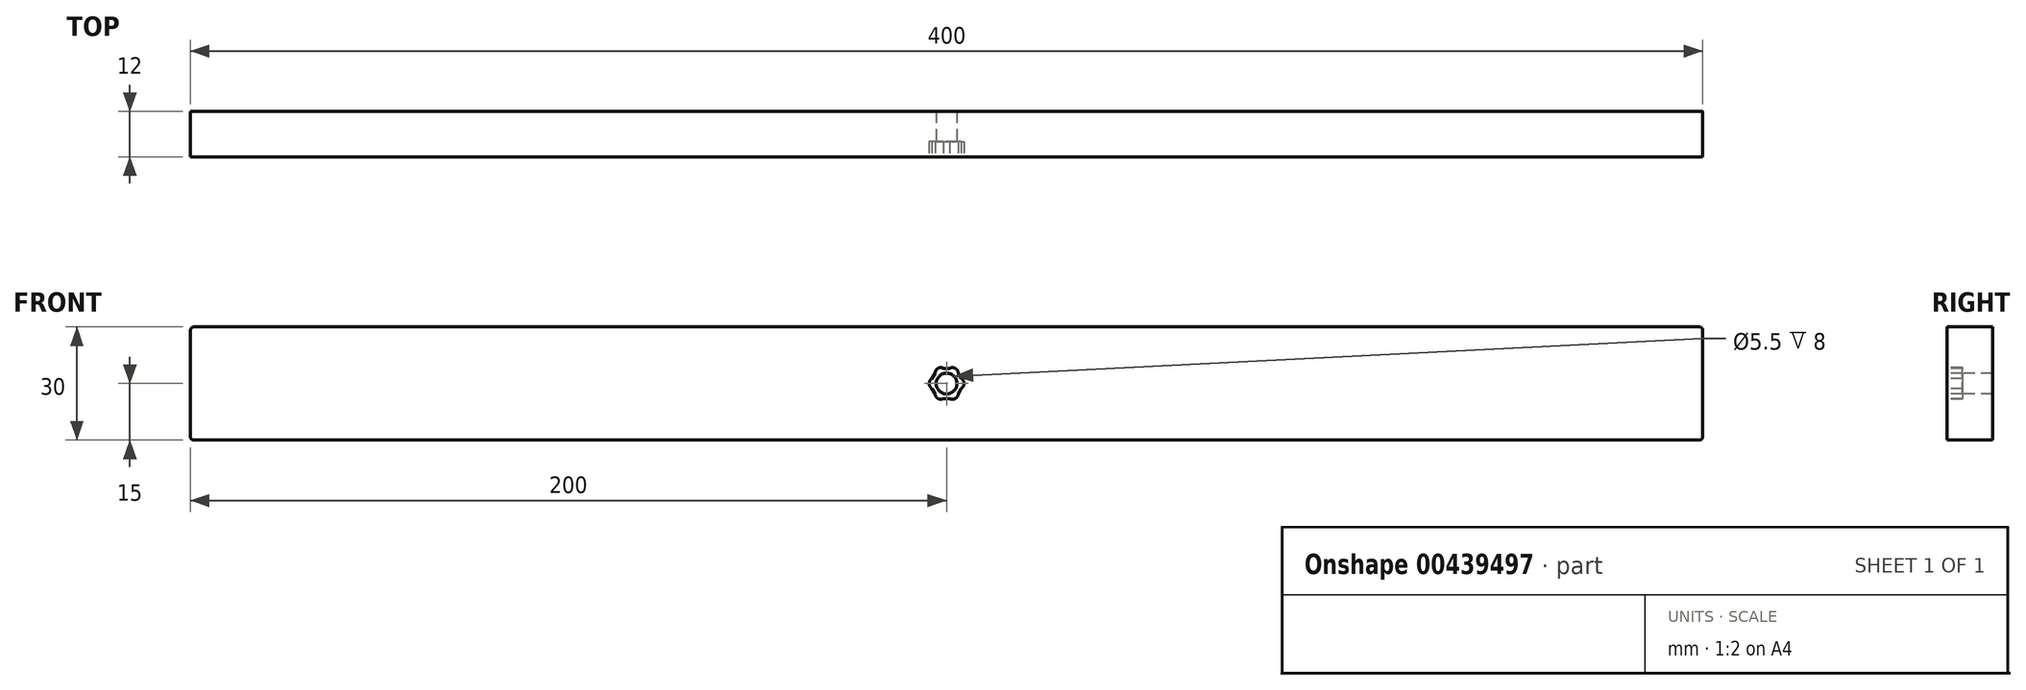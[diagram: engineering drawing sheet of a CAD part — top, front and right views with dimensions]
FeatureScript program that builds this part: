
annotation { "Feature Type Name" : "Feature", "Feature Type Description" : "" }
export const myFeature = defineFeature(function(context is Context, id is Id, definition is map)
    precondition{}
    {
        {
            var Q0;
            Q0=qCreatedBy(makeId("Right.planeOp"),FACE);
            var sketch = newSketch(context, id + "F0", { "sketchPlane" : qUnion([Q0])});
            skLineSegment(sketch, "E0.bottom", {"start": v(0, 0) * mm, "end": v(12, 0) * mm});
            skLineSegment(sketch, "E0.top", {"start": v(0, 30) * mm, "end": v(12, 30) * mm});
            skLineSegment(sketch, "E0.left", {"start": v(0, 0) * mm, "end": v(0, 30) * mm});
            skLineSegment(sketch, "E0.right", {"start": v(12, 0) * mm, "end": v(12, 30) * mm});
            skSolve(sketch);
        }
        {
            var Q0;
            Q0=makeQuery(id+"F0.imprint","IMPRINT",FACE,{"disambiguationData":[TD([[makeQuery(id+"F0.imprint","IMPRINT",EDGE,{"derivedFrom":sQuery(id+"F0.wireOp",EDGE,"E0.bottom")}),1.0]])]});
            extrude(context, id + "F1", {"entities" : qUnion([Q0]), "depth" : 400 * mm, "offsetDistance" : 25 * mm, "symmetric" : true});
        }
        {
            var Q0;
            Q0=makeQuery(id+"F1.opExtrude","CAP_EDGE",EDGE,{"disambiguationData":[OSD([sQuery(id+"F0.wireOp",EDGE,"E0.top")])],"isStart":true});
            var Q1;
            Q1=makeQuery(id+"F1.opExtrude","CAP_EDGE",EDGE,{"disambiguationData":[OSD([sQuery(id+"F0.wireOp",EDGE,"E0.top")])],"isStart":false});
            var Q2;
            Q2=makeQuery(id+"F1.opExtrude","CAP_EDGE",EDGE,{"disambiguationData":[OSD([sQuery(id+"F0.wireOp",EDGE,"E0.bottom")])],"isStart":false});
            var Q3;
            Q3=makeQuery(id+"F1.opExtrude","CAP_EDGE",EDGE,{"disambiguationData":[OSD([sQuery(id+"F0.wireOp",EDGE,"E0.bottom")])],"isStart":true});
            fillet(context, id + "F2", {"entities" : qUnion([Q0, Q1, Q2, Q3]), "tangentPropagation" : true, "radius" : 1 * mm, "defaultsChanged" : false, "vertexSettings" : [], "allowEdgeOverflow" : false});
        }
        {
            var Q0;
            Q0=makeQuery(id+"F1.opExtrude","SWEPT_FACE",FACE,{"disambiguationData":[OSD([sQuery(id+"F0.wireOp",EDGE,"E0.left")])]});
            var sketch = newSketch(context, id + "F3", { "sketchPlane" : qUnion([Q0])});
            skLineSegment(sketch, "E1", {"start": v(0, 0) * mm, "end": v(0, 30) * mm, "construction": true});
            skCircle(sketch, "E2.cCircle", {"center": v(0, 15) * mm, "radius": 4 * mm, "construction": true});
            skLineSegment(sketch, "E2.0", {"start": v(-2.3, 19) * mm, "end": v(0, 19) * mm, "construction": true});
            skLineSegment(sketch, "E2.1", {"start": v(2.3, 19) * mm, "end": v(3.06, 17.7) * mm, "construction": true});
            skLineSegment(sketch, "E2.3", {"start": v(2.3, 11) * mm, "end": v(-2.3, 11) * mm, "construction": true});
            skLineSegment(sketch, "E2.4", {"start": v(-2.3, 11) * mm, "end": v(-4.62, 15) * mm, "construction": true});
            skLineSegment(sketch, "E2.5", {"start": v(-4.62, 15) * mm, "end": v(-2.3, 19) * mm, "construction": true});
            skPoint(sketch, "E2.0.midPoint", {"position": v(0, 19) * mm});
            skArc(sketch, "E3", {"start": v(3.06, 17.7) * mm, "mid": v(2.3, 19) * mm, "end": v(0.8, 19) * mm});
            skLineSegment(sketch, "E4", {"start": v(1.56, 17.7) * mm, "end": v(0.8, 19) * mm});
            skLineSegment(sketch, "E5", {"start": v(0.8, 19) * mm, "end": v(2.3, 19) * mm, "construction": true});
            skLineSegment(sketch, "E6", {"start": v(3.06, 17.7) * mm, "end": v(3.46, 17) * mm});
            skLineSegment(sketch, "E7", {"start": v(0, 19) * mm, "end": v(0.8, 19) * mm});
            skLineSegment(sketch, "E8.1.0", {"start": v(3.87, 13.7) * mm, "end": v(3.46, 13) * mm});
            skArc(sketch, "E8.1.1", {"start": v(3.87, 13.7) * mm, "mid": v(4.62, 15) * mm, "end": v(3.87, 16.3) * mm});
            skLineSegment(sketch, "E8.1.2", {"start": v(3.46, 17) * mm, "end": v(3.87, 16.3) * mm});
            skLineSegment(sketch, "E8.2.0", {"start": v(0.8, 11) * mm, "end": v(0, 11) * mm});
            skArc(sketch, "E8.2.1", {"start": v(0.8, 11) * mm, "mid": v(2.3, 11) * mm, "end": v(3.06, 12.3) * mm});
            skLineSegment(sketch, "E8.2.2", {"start": v(3.46, 13) * mm, "end": v(3.06, 12.3) * mm});
            skLineSegment(sketch, "E8.anchor1", {"start": v(0, 15) * mm, "end": v(0, 19) * mm, "construction": true});
            skLineSegment(sketch, "E8.anchor2", {"start": v(0, 15) * mm, "end": v(3.46, 13) * mm, "construction": true});
            skLineSegment(sketch, "E9.MirrorCS", {"start": v(0, 19) * mm, "end": v(-0.8, 19) * mm});
            skArc(sketch, "E10.MirrorCS", {"start": v(-3.06, 17.7) * mm, "mid": v(-2.3, 19) * mm, "end": v(-0.8, 19) * mm});
            skLineSegment(sketch, "E11.MirrorCS", {"start": v(-3.06, 17.7) * mm, "end": v(-3.46, 17) * mm});
            skLineSegment(sketch, "E12.MirrorCS", {"start": v(-3.46, 13) * mm, "end": v(-3.06, 12.3) * mm});
            skArc(sketch, "E13.MirrorCS", {"start": v(-0.8, 11) * mm, "mid": v(-2.3, 11) * mm, "end": v(-3.06, 12.3) * mm});
            skLineSegment(sketch, "E14.MirrorCS", {"start": v(-3.87, 13.7) * mm, "end": v(-3.46, 13) * mm});
            skLineSegment(sketch, "E15.MirrorCS", {"start": v(-3.46, 17) * mm, "end": v(-3.87, 16.3) * mm});
            skArc(sketch, "E16.MirrorCS", {"start": v(-3.87, 13.7) * mm, "mid": v(-4.62, 15) * mm, "end": v(-3.87, 16.3) * mm});
            skLineSegment(sketch, "E17", {"start": v(-0.8, 11) * mm, "end": v(0.8, 11) * mm});
            skCircle(sketch, "E18", {"center": v(0, 15) * mm, "radius": 2.75 * mm});
            skSolve(sketch);
        }
        {
            var Q0;
            Q0 = qSketchRegion(id + "F3", true);
            extrude(context, id + "F4", {"entities" : qUnion([Q0]), "operationType" : NewBodyOperationType.REMOVE, "oppositeDirection" : true, "depth" : 4 * mm, "offsetDistance" : 25 * mm});
        }
        {
            var Q0;
            Q0=makeQuery(id+"F4.boolean.opBoolean","SPLIT",FACE,{"disambiguationData":[TD([makeQuery(id+"F4.opExtrude","SWEPT_FACE",FACE,{"disambiguationData":[OSD([sQuery(id+"F3.wireOp",EDGE,"E18")])]})])],"derivedFrom":makeQuery(id+"F1.opExtrude","SWEPT_FACE",FACE,{"disambiguationData":[OSD([sQuery(id+"F0.wireOp",EDGE,"E0.left")])]})});
            extrude(context, id + "F5", {"entities" : qUnion([Q0]), "operationType" : NewBodyOperationType.REMOVE, "endBound" : BoundingType.THROUGH_ALL, "oppositeDirection" : true, "depth" : 25 * mm, "offsetDistance" : 25 * mm});
        }
    });
